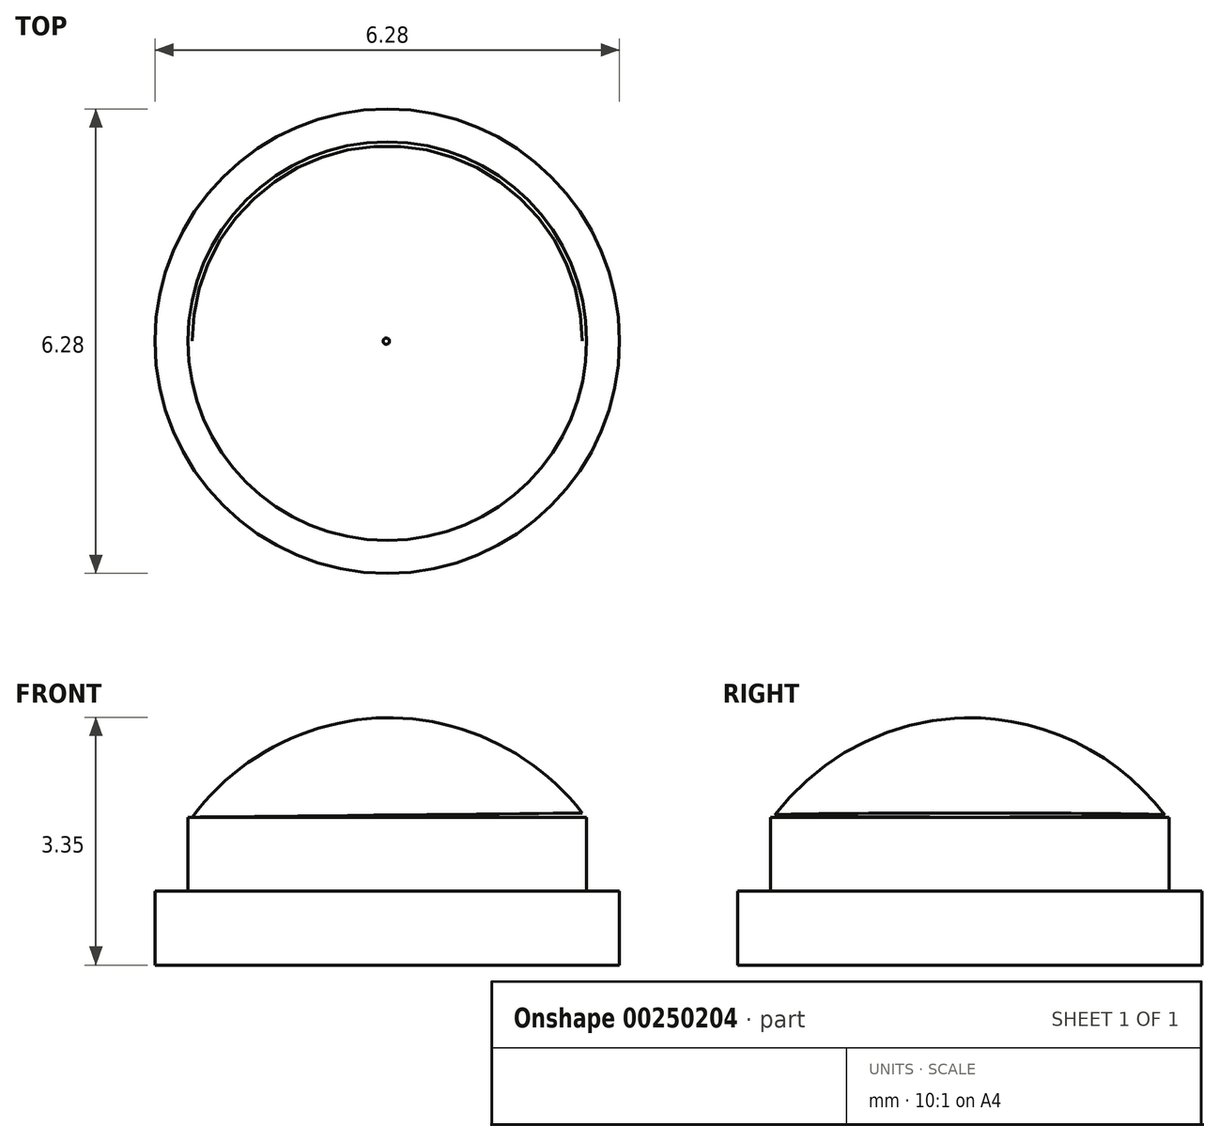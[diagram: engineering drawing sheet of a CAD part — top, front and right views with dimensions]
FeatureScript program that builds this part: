
annotation { "Feature Type Name" : "Feature", "Feature Type Description" : "" }
export const myFeature = defineFeature(function(context is Context, id is Id, definition is map)
    precondition{}
    {
        {
            var Q0;
            Q0=qCreatedBy(makeId("Top.planeOp"),FACE);
            var sketch = newSketch(context, id + "F0", { "sketchPlane" : qUnion([Q0])});
            skCircle(sketch, "E0", {"center": v(0, 0) * mm, "radius": 3.14 * mm});
            skSolve(sketch);
        }
        {
            var Q0;
            Q0=makeQuery(id+"F0.imprint","IMPRINT",FACE,{"disambiguationData":[TD([[makeQuery(id+"F0.imprint","IMPRINT",EDGE,{"derivedFrom":sQuery(id+"F0.wireOp",EDGE,"E0")}),1.0]])]});
            extrude(context, id + "F1", {"entities" : qUnion([Q0]), "depth" : 1 * mm});
        }
        {
            var Q0;
            Q0=makeQuery(id+"F1.opExtrude","CAP_FACE",FACE,{"disambiguationData":[OSD([sQuery(id+"F0.wireOp",EDGE,"E0")])],"isStart":false});
            var sketch = newSketch(context, id + "F2", { "sketchPlane" : qUnion([Q0])});
            skCircle(sketch, "E1", {"center": v(0, 0) * mm, "radius": 2.7 * mm});
            skSolve(sketch);
        }
        {
            var Q0;
            Q0=makeQuery(id+"F2.imprint","IMPRINT",FACE,{"disambiguationData":[TD([[makeQuery(id+"F2.imprint","IMPRINT",EDGE,{"derivedFrom":sQuery(id+"F2.wireOp",EDGE,"E1")}),1.0]])]});
            extrude(context, id + "F3", {"entities" : qUnion([Q0]), "operationType" : NewBodyOperationType.ADD, "depth" : 1 * mm});
        }
        {
            var Q0;
            Q0=qCreatedBy(makeId("Front.planeOp"),FACE);
            var sketch = newSketch(context, id + "F4", { "sketchPlane" : qUnion([Q0])});
            skArc(sketch, "E2", {"start": v(-2.68, 2) * mm, "mid": v(-0.04, 3.35) * mm, "end": v(2.64, 2.06) * mm});
            skLineSegment(sketch, "E3", {"start": v(2.64, 2.06) * mm, "end": v(-2.68, 2) * mm});
            skLineSegment(sketch, "E4", {"start": v(0, 2.03) * mm, "end": v(-0.01, 3.35) * mm});
            skSolve(sketch);
        }
        {
            var Q0;
            {var subQ3=sQuery(id+"F4.wireOp",EDGE,"E4");Q0=makeQuery(id+"F4.imprint","IMPRINT",FACE,{"disambiguationData":[TD([[makeQuery(id+"F4.imprint","IMPRINT",EDGE,{"derivedFrom":subQ3}),-1.0]])]});}
            var Q1;
            Q1=sQuery(id+"F4.wireOp",EDGE,"E4");
            revolve(context, id + "F5", {"entities" : qUnion([Q0]), "axis" : qUnion([Q1]), "revolveType" : RevolveType.FULL});
        }
    });
